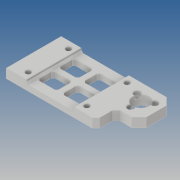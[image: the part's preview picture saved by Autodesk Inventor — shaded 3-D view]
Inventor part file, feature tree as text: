
AUTODESK INVENTOR PART (.ipt)
format: ipt  version: 2019 (Build 230136000, 136)  size: 278,528 bytes
history: native  units: mm
features: sketch x7, extrude x5, projected_geometry x5, chamfer x4, hole x2, pattern_circular x1
ambient origin geometry x8: Origin, YZ Plane, XZ Plane, XY Plane, X Axis, Y Axis, Z Axis, Center Point
bodies: Solide1 (feature_tree)
feature tree (24):
  extrude  "Extrusion1"  Depth=123.0mm
  extrude  "Extrusion2"  Depth=60.0mm
  hole  "Perçage1"  [1 undecoded]
  pattern_circular  "Réseau circulaire1"  [2 undecoded]
  hole  "Perçage2"  [1 undecoded]
  extrude  "Extrusion4"  Depth=18.0mm
  chamfer  "Chanfrein1"  Distance=10.0mm
  extrude  "Extrusion5"  Depth=11.0mm
  chamfer  "Chanfrein5"  Distance=30.0mm Angle=360.0deg
  extrude  "Extrusion6"  Depth=22.0mm
  chamfer  "Chanfrein6"  Distance=11.0mm
  chamfer  "Chanfrein7"  Distance=9.0mm
  sketch  "Esquisse1"
  sketch  "Esquisse2"
  projected_geometry  "Boucle projetée1"
  sketch  "Esquisse4"
  projected_geometry  "Boucle projetée3"
  sketch  "Esquisse5"
  projected_geometry  "Boucle projetée4"
  sketch  "Esquisse6"
  projected_geometry  "Boucle projetée5"
  sketch  "Esquisse7"
  projected_geometry  "Boucle projetée6"
  sketch  "Esquisse8"
note: 4 required parameter values undecoded (feature->parameter linkage not recoverable at this tier; creation-order binding heuristic only, values carry confidence <= 0.55)
